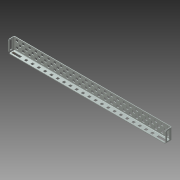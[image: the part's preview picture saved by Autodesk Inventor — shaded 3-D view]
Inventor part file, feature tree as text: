
AUTODESK INVENTOR PART (.ipt)
format: ipt  version: 2013 (Build 170138000, 138)  size: 1,944,064 bytes
history: native  units: mm (DEFAULTED — no unit token found)
features: other x103, extrude x103, sketch x4, pattern_linear x3, imported_body x1
ambient origin geometry x8: Origin, YZ Plane, XZ Plane, XY Plane, X Axis, Y Axis, Z Axis, Center Point
bodies: Solid1 (feature_tree)
feature tree (214):
  imported_body  "Base1"
  sketch  "Sketch1"  dims[d2=1.1684mm]
  pattern_linear  "Rectangular Pattern1"  Count1=25  [1 undecoded]
  pattern_linear  "Rectangular Pattern2"  Spacing1=12.7mm  [1 undecoded]
  sketch  "Sketch2"  dims[d3=0.0mm]
  sketch  "Sketch3"  dims[d4=1.1684mm]
  pattern_linear  "Rectangular Pattern3"  Count1=2 Spacing1=12.7mm
  other  "Srf1"
  other  "Srf2"
  other  "Srf3"
  other  "Srf4"
  other  "Srf5"
  other  "Srf6"
  other  "Srf7"
  other  "Srf8"
  other  "Srf9"
  other  "Srf10"
  other  "Srf11"
  other  "Srf12"
  other  "Srf13"
  other  "Srf14"
  other  "Srf15"
  other  "Srf16"
  other  "Srf17"
  other  "Srf18"
  other  "Srf19"
  other  "Srf20"
  other  "Srf21"
  other  "Srf22"
  other  "Srf23"
  other  "Srf24"
  other  "Srf25"
  other  "Srf26"
  other  "Srf27"
  other  "Srf28"
  other  "Srf29"
  other  "Srf30"
  other  "Srf31"
  other  "Srf32"
  other  "Srf33"
  other  "Srf34"
  other  "Srf35"
  other  "Srf36"
  other  "Srf37"
  other  "Srf38"
  other  "Srf39"
  other  "Srf40"
  other  "Srf41"
  other  "Srf42"
  other  "Srf43"
  other  "Srf44"
  other  "Srf45"
  other  "Srf46"
  other  "Srf47"
  other  "Srf48"
  other  "Srf49"
  other  "Srf50"
  other  "Srf51"
  other  "Srf52"
  other  "Srf53"
  other  "Srf54"
  other  "Srf55"
  other  "Srf56"
  other  "Srf57"
  other  "Srf58"
  other  "Srf59"
  other  "Srf60"
  other  "Srf61"
  other  "Srf62"
  other  "Srf63"
  other  "Srf64"
  other  "Srf65"
  other  "Srf66"
  other  "Srf67"
  other  "Srf68"
  other  "Srf69"
  other  "Srf70"
  other  "Srf71"
  other  "Srf72"
  other  "Srf73"
  other  "Srf74"
  other  "Srf75"
  other  "Srf76"
  other  "Srf77"
  other  "Srf78"
  sketch  "Sketch4"  dims[d5=0.0mm d6=250.0mm d8=12.7mm d9=20.0mm d11=12.7mm d12=240.0mm d14=12.7mm d15=1.1684mm d16=0.0mm d17=1.1684mm d18=0.0mm d19=1.1684mm d20=0.0mm d21=1.1684mm d22=0.0mm d23=1.1684mm d24=0.0mm d25=250.0mm d27=12.7mm d28=0.0mm d29=0.0mm d30=0.0mm d31=0.0mm d32=0.0mm d33=0.0mm d34=0.0mm d35=0.0mm d36=0.0mm d37=0.0mm d38=0.0mm d39=0.0mm d40=0.0mm d41=0.0mm d42=0.0mm d43=0.0mm d44=0.0mm d45=0.0mm d46=0.0mm d47=0.0mm d48=0.0mm d49=0.0mm d50=0.0mm d51=0.0mm d52=0.0mm d53=0.0mm d54=0.0mm d55=0.0mm d56=0.0mm d57=0.0mm d58=0.0mm d59=0.0mm d60=0.0mm d61=0.0mm d62=0.0mm d63=0.0mm d64=0.0mm d65=0.0mm d66=0.0mm d67=0.0mm d68=0.0mm d69=0.0mm d70=0.0mm d71=0.0mm d72=0.0mm d73=0.0mm d74=0.0mm d75=0.0mm d76=0.0mm d77=0.0mm d78=0.0mm d79=0.0mm d80=0.0mm d81=0.0mm d82=0.0mm d83=0.0mm d84=0.0mm d85=0.0mm d86=0.0mm d87=0.0mm d88=0.0mm d89=0.0mm d90=0.0mm d91=0.0mm d92=0.0mm d93=0.0mm d94=0.0mm d95=0.0mm d96=0.0mm d97=0.0mm d98=0.0mm d99=0.0mm d100=0.0mm d101=0.0mm d102=0.0mm d103=0.0mm d104=0.0mm d105=0.0mm d106=0.0mm d107=0.0mm d108=0.0mm d109=0.0mm d110=0.0mm d111=0.0mm d112=0.0mm d113=0.0mm d114=0.0mm d115=0.0mm d116=0.0mm d117=0.0mm d118=0.0mm d119=0.0mm d120=0.0mm d121=0.0mm d122=0.0mm d123=0.0mm d124=0.0mm d125=0.0mm d126=0.0mm d127=0.0mm d128=0.0mm d129=0.0mm d130=0.0mm d131=0.0mm d132=0.0mm d133=0.0mm d134=0.0mm d135=0.0mm d136=0.0mm d137=0.0mm d138=0.0mm d139=0.0mm d140=0.0mm d141=0.0mm d142=0.0mm d143=0.0mm d144=0.0mm d145=0.0mm d146=0.0mm d147=0.0mm d148=0.0mm d149=0.0mm d150=0.0mm d151=0.0mm d152=0.0mm d153=0.0mm d154=0.0mm d155=0.0mm d156=0.0mm d157=0.0mm d158=0.0mm d159=0.0mm d160=0.0mm d161=0.0mm d162=0.0mm d163=0.0mm d164=0.0mm d165=0.0mm d166=0.0mm d167=0.0mm d168=0.0mm d169=0.0mm d170=0.0mm d171=0.0mm d172=0.0mm d173=0.0mm d174=0.0mm d175=0.0mm d176=0.0mm d177=0.0mm d178=0.0mm d179=0.0mm d180=0.0mm d181=0.0mm d182=0.0mm d183=0.0mm d184=0.0mm d185=0.0mm d186=0.0mm d187=0.0mm d188=0.0mm d189=0.0mm d190=0.0mm d191=0.0mm d192=0.0mm d193=0.0mm d194=0.0mm d195=0.0mm d196=0.0mm d197=0.0mm d198=0.0mm d199=0.0mm d200=0.0mm d201=0.0mm d202=0.0mm d203=0.0mm d204=0.0mm d205=0.0mm d206=0.0mm d207=0.0mm d208=0.0mm d209=0.0mm d210=0.0mm d211=0.0mm d212=0.0mm d213=0.0mm d214=0.0mm d215=0.0mm d216=0.0mm d217=0.0mm d218=0.0mm d219=0.0mm d220=0.0mm d221=0.0mm d222=0.0mm d223=0.0mm d224=0.0mm d225=0.0mm d226=0.0mm d227=0.0mm d228=0.0mm d229=0.0mm d230=0.0mm d231=0.0mm d232=0.0mm d233=0.0mm]
  other  "Srf79"
  other  "Srf80"
  other  "Srf81"
  other  "Srf82"
  other  "Srf83"
  other  "Srf84"
  other  "Srf85"
  other  "Srf86"
  other  "Srf87"
  other  "Srf88"
  other  "Srf89"
  other  "Srf90"
  other  "Srf91"
  other  "Srf92"
  other  "Srf93"
  other  "Srf94"
  other  "Srf95"
  other  "Srf96"
  other  "Srf97"
  other  "Srf98"
  other  "Srf99"
  other  "Srf100"
  other  "Srf101"
  other  "Srf102"
  other  "Srf103"
  extrude  "ExtrusionSrf1"  Depth=240.0mm
  extrude  "ExtrusionSrf2"  Depth=12.7mm
  extrude  "ExtrusionSrf75"  Depth=1.1684mm
  extrude  "ExtrusionSrf76"  TaperAngle=0.0deg  [1 undecoded]
  extrude  "ExtrusionSrf77"  Depth=1.1684mm
  extrude  "ExtrusionSrf78"  TaperAngle=0.0deg  [1 undecoded]
  extrude  "ExtrusionSrf79"  Depth=1.1684mm
  extrude  "ExtrusionSrf3"  TaperAngle=0.0deg  [1 undecoded]
  extrude  "ExtrusionSrf4"  Depth=1.1684mm
  extrude  "ExtrusionSrf5"  TaperAngle=0.0deg  [1 undecoded]
  extrude  "ExtrusionSrf6"  Depth=1.1684mm
  extrude  "ExtrusionSrf7"  TaperAngle=0.0deg  [1 undecoded]
  extrude  "ExtrusionSrf8"  Depth=250.0mm
  extrude  "ExtrusionSrf9"  Depth=12.7mm
  extrude  "ExtrusionSrf10"  TaperAngle=0.0deg  [1 undecoded]
  extrude  "ExtrusionSrf11"  TaperAngle=0.0deg  [1 undecoded]
  extrude  "ExtrusionSrf12"  TaperAngle=0.0deg  [1 undecoded]
  extrude  "ExtrusionSrf13"  TaperAngle=0.0deg  [1 undecoded]
  extrude  "ExtrusionSrf14"  TaperAngle=0.0deg  [1 undecoded]
  extrude  "ExtrusionSrf15"  TaperAngle=0.0deg  [1 undecoded]
  extrude  "ExtrusionSrf16"  TaperAngle=0.0deg  [1 undecoded]
  extrude  "ExtrusionSrf17"  TaperAngle=0.0deg  [1 undecoded]
  extrude  "ExtrusionSrf18"  TaperAngle=0.0deg  [1 undecoded]
  extrude  "ExtrusionSrf19"  TaperAngle=0.0deg  [1 undecoded]
  extrude  "ExtrusionSrf20"  TaperAngle=0.0deg  [1 undecoded]
  extrude  "ExtrusionSrf21"  TaperAngle=0.0deg  [1 undecoded]
  extrude  "ExtrusionSrf22"  TaperAngle=0.0deg  [1 undecoded]
  extrude  "ExtrusionSrf23"  TaperAngle=0.0deg  [1 undecoded]
  extrude  "ExtrusionSrf24"  TaperAngle=0.0deg  [1 undecoded]
  extrude  "ExtrusionSrf25"  TaperAngle=0.0deg  [1 undecoded]
  extrude  "ExtrusionSrf26"  TaperAngle=0.0deg  [1 undecoded]
  extrude  "ExtrusionSrf27"  TaperAngle=0.0deg  [1 undecoded]
  extrude  "ExtrusionSrf28"  TaperAngle=0.0deg  [1 undecoded]
  extrude  "ExtrusionSrf29"  TaperAngle=0.0deg  [1 undecoded]
  extrude  "ExtrusionSrf30"  TaperAngle=0.0deg  [1 undecoded]
  extrude  "ExtrusionSrf31"  TaperAngle=0.0deg  [1 undecoded]
  extrude  "ExtrusionSrf32"  TaperAngle=0.0deg  [1 undecoded]
  extrude  "ExtrusionSrf33"  TaperAngle=0.0deg  [1 undecoded]
  extrude  "ExtrusionSrf34"  TaperAngle=0.0deg  [1 undecoded]
  extrude  "ExtrusionSrf35"  TaperAngle=0.0deg  [1 undecoded]
  extrude  "ExtrusionSrf36"  TaperAngle=0.0deg  [1 undecoded]
  extrude  "ExtrusionSrf37"  TaperAngle=0.0deg  [1 undecoded]
  extrude  "ExtrusionSrf38"  TaperAngle=0.0deg  [1 undecoded]
  extrude  "ExtrusionSrf39"  TaperAngle=0.0deg  [1 undecoded]
  extrude  "ExtrusionSrf40"  TaperAngle=0.0deg  [1 undecoded]
  extrude  "ExtrusionSrf41"  TaperAngle=0.0deg  [1 undecoded]
  extrude  "ExtrusionSrf42"  TaperAngle=0.0deg  [1 undecoded]
  extrude  "ExtrusionSrf43"  TaperAngle=0.0deg  [1 undecoded]
  extrude  "ExtrusionSrf44"  TaperAngle=0.0deg  [1 undecoded]
  extrude  "ExtrusionSrf45"  TaperAngle=0.0deg  [1 undecoded]
  extrude  "ExtrusionSrf46"  TaperAngle=0.0deg  [1 undecoded]
  extrude  "ExtrusionSrf47"  TaperAngle=0.0deg  [1 undecoded]
  extrude  "ExtrusionSrf48"  TaperAngle=0.0deg  [1 undecoded]
  extrude  "ExtrusionSrf49"  TaperAngle=0.0deg  [1 undecoded]
  extrude  "ExtrusionSrf50"  TaperAngle=0.0deg  [1 undecoded]
  extrude  "ExtrusionSrf51"  TaperAngle=0.0deg  [1 undecoded]
  extrude  "ExtrusionSrf52"  TaperAngle=0.0deg  [1 undecoded]
  extrude  "ExtrusionSrf53"  TaperAngle=0.0deg  [1 undecoded]
  extrude  "ExtrusionSrf54"  TaperAngle=0.0deg  [1 undecoded]
  extrude  "ExtrusionSrf55"  TaperAngle=0.0deg  [1 undecoded]
  extrude  "ExtrusionSrf56"  TaperAngle=0.0deg  [1 undecoded]
  extrude  "ExtrusionSrf57"  TaperAngle=0.0deg  [1 undecoded]
  extrude  "ExtrusionSrf58"  TaperAngle=0.0deg  [1 undecoded]
  extrude  "ExtrusionSrf59"  TaperAngle=0.0deg  [1 undecoded]
  extrude  "ExtrusionSrf60"  TaperAngle=0.0deg  [1 undecoded]
  extrude  "ExtrusionSrf61"  TaperAngle=0.0deg  [1 undecoded]
  extrude  "ExtrusionSrf62"  TaperAngle=0.0deg  [1 undecoded]
  extrude  "ExtrusionSrf63"  TaperAngle=0.0deg  [1 undecoded]
  extrude  "ExtrusionSrf64"  TaperAngle=0.0deg  [1 undecoded]
  extrude  "ExtrusionSrf65"  TaperAngle=0.0deg  [1 undecoded]
  extrude  "ExtrusionSrf66"  TaperAngle=0.0deg  [1 undecoded]
  extrude  "ExtrusionSrf67"  TaperAngle=0.0deg  [1 undecoded]
  extrude  "ExtrusionSrf68"  TaperAngle=0.0deg  [1 undecoded]
  extrude  "ExtrusionSrf69"  TaperAngle=0.0deg  [1 undecoded]
  extrude  "ExtrusionSrf70"  TaperAngle=0.0deg  [1 undecoded]
  extrude  "ExtrusionSrf71"  TaperAngle=0.0deg  [1 undecoded]
  extrude  "ExtrusionSrf72"  TaperAngle=0.0deg  [1 undecoded]
  extrude  "ExtrusionSrf73"  TaperAngle=0.0deg  [1 undecoded]
  extrude  "ExtrusionSrf74"  TaperAngle=0.0deg  [1 undecoded]
  extrude  "ExtrusionSrf80"  TaperAngle=0.0deg  [1 undecoded]
  extrude  "ExtrusionSrf81"  TaperAngle=0.0deg  [1 undecoded]
  extrude  "ExtrusionSrf82"  TaperAngle=0.0deg  [1 undecoded]
  extrude  "ExtrusionSrf83"  TaperAngle=0.0deg  [1 undecoded]
  extrude  "ExtrusionSrf84"  TaperAngle=0.0deg  [1 undecoded]
  extrude  "ExtrusionSrf85"  TaperAngle=0.0deg  [1 undecoded]
  extrude  "ExtrusionSrf86"  TaperAngle=0.0deg  [1 undecoded]
  extrude  "ExtrusionSrf87"  TaperAngle=0.0deg  [1 undecoded]
  extrude  "ExtrusionSrf88"  TaperAngle=0.0deg  [1 undecoded]
  extrude  "ExtrusionSrf89"  TaperAngle=0.0deg  [1 undecoded]
  extrude  "ExtrusionSrf90"  TaperAngle=0.0deg  [1 undecoded]
  extrude  "ExtrusionSrf91"  TaperAngle=0.0deg  [1 undecoded]
  extrude  "ExtrusionSrf92"  TaperAngle=0.0deg  [1 undecoded]
  extrude  "ExtrusionSrf93"  TaperAngle=0.0deg  [1 undecoded]
  extrude  "ExtrusionSrf94"  TaperAngle=0.0deg  [1 undecoded]
  extrude  "ExtrusionSrf95"  TaperAngle=0.0deg  [1 undecoded]
  extrude  "ExtrusionSrf96"  TaperAngle=0.0deg  [1 undecoded]
  extrude  "ExtrusionSrf97"  TaperAngle=0.0deg  [1 undecoded]
  extrude  "ExtrusionSrf98"  TaperAngle=0.0deg  [1 undecoded]
  extrude  "ExtrusionSrf99"  TaperAngle=0.0deg  [1 undecoded]
  extrude  "ExtrusionSrf100"  TaperAngle=0.0deg  [1 undecoded]
  extrude  "ExtrusionSrf101"  TaperAngle=0.0deg  [1 undecoded]
  extrude  "ExtrusionSrf102"  TaperAngle=0.0deg  [1 undecoded]
  extrude  "ExtrusionSrf103"  TaperAngle=0.0deg  [1 undecoded]
note: 96 required parameter values undecoded (feature->parameter linkage not recoverable at this tier; creation-order binding heuristic only, values carry confidence <= 0.55)
